# Revit family: GD1 Rectangular Poseur Height
name_source: partatom
category: Furniture
units: mm (PartAtom-declared; Revit-internal decimal feet)

## family parameters
Always vertical = Yes
Cut with Voids When Loaded = No
OmniClass Number = 23.40.20.00
OmniClass Title = General Furniture and Specialties
Room Calculation Point = No
Shared = No
Work Plane-Based = No

## types (6) — shared parameters
Assembly Code = E2020200
Frame = Gresham - Black Metal
Manufacturer = Gresham Office Furniture
Range = GD1
Table Top = Gresham - White MFC
URL = www.gof.co.uk

## per-type parameters (varying)
| type | Depth | Power Module | Product Code | Width |
| 2000 x 1000 | 1000 mm  [stored 3.28084 ft] | No | GD1A2 | 2000 mm  [stored 6.56168 ft] |
| 2400 x 1200 | 1200 mm  [stored 3.93701 ft] | No | GD1B2 | 2400 mm |
| 2800 x 1200 | 1200 mm  [stored 3.93701 ft] | No | GD1C2 | 2800 mm  [stored 9.18635 ft] |
| 2000 x 1000 C/W Power | 1000 mm  [stored 3.28084 ft] | Yes | GD1A4 | 2000 mm  [stored 6.56168 ft] |
| 2400 x 1200 C/W Power | 1200 mm  [stored 3.93701 ft] | Yes | GD1B4 | 2400 mm |
| 2800 x 1200 C/W Power | 1200 mm  [stored 3.93701 ft] | Yes | GD1C4 | 2800 mm  [stored 9.18635 ft] |

note: [stored X ft] marks values corroborated as IEEE doubles in the binary element streams (Revit-internal decimal feet)

## geometry (parser evidence)
native form markers: Sweep x4
no freeform markers — native parametric forms only
